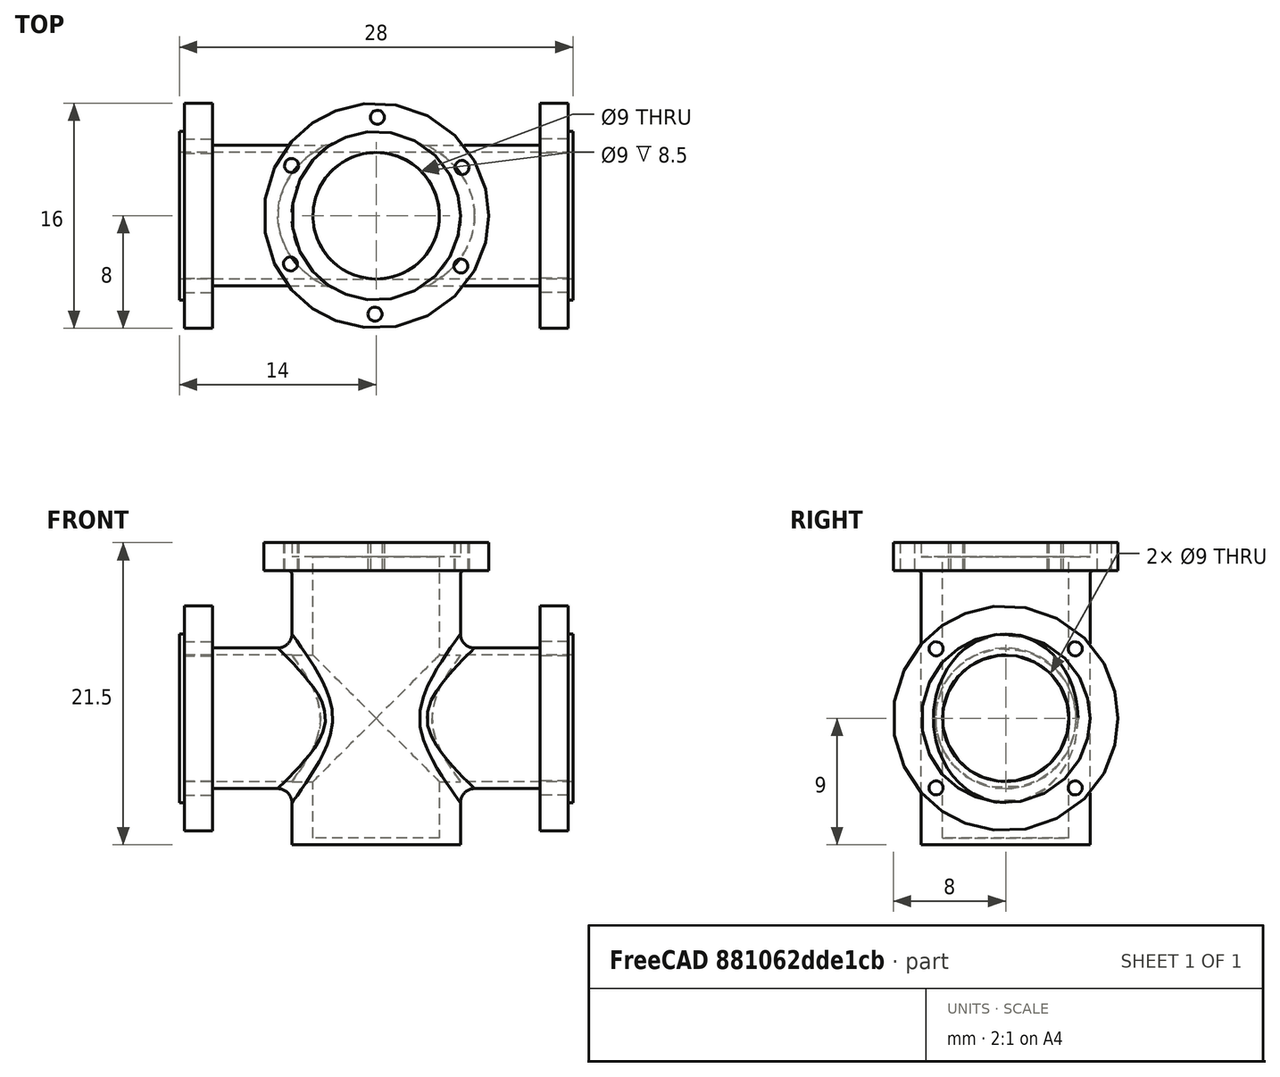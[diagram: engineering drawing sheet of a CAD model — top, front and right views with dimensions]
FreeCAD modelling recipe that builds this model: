
FCSTD DOCUMENT  (FreeCAD 0.17R9652 (Git))
Label: Moderate
License: All rights reserved
LicenseURL: http://en.wikipedia.org/wiki/All_rights_reserved
objects: Sketcher::SketchObject×10, PartDesign::Pad×5, PartDesign::Pocket×5, PartDesign::Mirrored×3, PartDesign::Plane×2, PartDesign::Body×2, PartDesign::Fillet×2, PartDesign::PolarPattern×1, PartDesign::Boolean×1
note: 41 computed .brp shape members not serialized (recipe doc carries the construction recipe); baked Part::Feature solids carry a one-line shape summary decoded from their .brp

FEATURE [Sketcher::SketchObject] Sketch
  MapMode = 5
  Support = -> [XY_Plane]
  sketch-geometry (1):
    g0: Circle CenterX=0 CenterY=0 CenterZ=0 NormalX=0 NormalY=0 NormalZ=1 Radius=6
  constraints (2):
    c: Coincident(g0,g-1)
    c: Radius(g0) = 6
FEATURE [PartDesign::Pad] Pad
  Length = 12
  Length2 = 9
  Midplane = true
  Profile = -> Sketch
  Type = 4
FEATURE [PartDesign::Plane] DatumPlane
  MapMode = 5
  Placement = pos=(0,0,12.5) rot=(0,0,1;0rad)
  Support = -> [XY_Plane]
  superPlacement = pos=(0,0,12.5) rot=(0,0,1;0rad)
FEATURE [Sketcher::SketchObject] Sketch001
  MapMode = 5
  Placement = pos=(0,0,12.5) rot=(0,0,1;0rad)
  Support = -> [DatumPlane]
  sketch-geometry (1):
    g0: Circle CenterX=0 CenterY=0 CenterZ=0 NormalX=0 NormalY=0 NormalZ=1 Radius=8
  constraints (2):
    c: Coincident(g0,g-1)
    c: Radius(g0) = 8
FEATURE [PartDesign::Pad] Pad001
  BaseFeature = -> Pad
  Length = 2
  Length2 = 100
  Profile = -> Sketch001
  Reversed = true
  Type = 0
FEATURE [PartDesign::Body] Body001
  Origin = -> Body001Origin
FEATURE [Sketcher::SketchObject] Sketch005
  MapMode = 5
  Placement = pos=(0,0,0) rot=(0.57735,0.57735,0.57735;2.0944rad)
  Support = -> [YZ_Plane]
  sketch-geometry (1):
    g0: Circle CenterX=0 CenterY=0 CenterZ=0 NormalX=0 NormalY=0 NormalZ=1 Radius=5
  constraints (2):
    c: Coincident(g0,g-1)
    c: Radius(g0) = 5
FEATURE [PartDesign::Pad] Pad002
  Length = 28
  Length2 = 100
  Midplane = true
  Placement = pos=(0,0,0) rot=(0.57735,0.57735,0.57735;2.0944rad)
  Profile = -> Sketch005
  Type = 0
FEATURE [PartDesign::Plane] DatumPlane001
  MapMode = 5
  Placement = pos=(13.65,0,0) rot=(0.57735,0.57735,0.57735;2.0944rad)
  Support = -> [YZ_Plane001]
  superPlacement = pos=(0,0,13.65) rot=(0,0,1;0rad)
FEATURE [Sketcher::SketchObject] Sketch006
  MapMode = 5
  Placement = pos=(13.65,0,0) rot=(0.57735,0.57735,0.57735;2.0944rad)
  Support = -> [DatumPlane001]
  sketch-geometry (1):
    g0: Circle CenterX=0 CenterY=0 CenterZ=0 NormalX=0 NormalY=0 NormalZ=1 Radius=6
  constraints (2):
    c: Coincident(g0,g-1)
    c: Radius(g0) = 6
FEATURE [PartDesign::Pad] Pad003
  BaseFeature = -> Pad002
  Length = 0.35
  Length2 = 100
  Placement = pos=(0,0,0) rot=(0.57735,0.57735,0.57735;2.0944rad)
  Profile = -> Sketch006
  Type = 0
FEATURE [PartDesign::Mirrored] Mirrored
  BaseFeature = -> Pad003
  MirrorPlane = -> YZ_Plane001
  Originals = -> [Pad003]
  Placement = pos=(0,0,0) rot=(0.57735,0.57735,0.57735;2.0944rad)
FEATURE [Sketcher::SketchObject] Sketch007
  MapMode = 5
  Placement = pos=(13.65,0,0) rot=(0.57735,0.57735,0.57735;2.0944rad)
  Support = -> [DatumPlane001]
  sketch-geometry (1):
    g0: Circle CenterX=0 CenterY=0 CenterZ=0 NormalX=0 NormalY=0 NormalZ=1 Radius=8
  constraints (2):
    c: Coincident(g0,g-1)
    c: Radius(g0) = 8
FEATURE [PartDesign::Pad] Pad004
  BaseFeature = -> Mirrored
  Length = 2
  Length2 = 100
  Placement = pos=(0,0,0) rot=(0.57735,0.57735,0.57735;2.0944rad)
  Profile = -> Sketch007
  Reversed = true
  Type = 0
FEATURE [PartDesign::Mirrored] Mirrored001
  BaseFeature = -> Pad004
  MirrorPlane = -> YZ_Plane001
  Originals = -> [Pad004]
  Placement = pos=(0,0,0) rot=(0.57735,0.57735,0.57735;2.0944rad)
FEATURE [Sketcher::SketchObject] Sketch008
  MapMode = 5
  Placement = pos=(13.65,0,0) rot=(0.57735,0.57735,0.57735;2.0944rad)
  Support = -> [DatumPlane001]
  sketch-geometry (9):
    g0: LineSegment [constr] StartX=-4.94975 StartY=4.94975 StartZ=0 EndX=-4.94975 EndY=-4.94975 EndZ=0
    g1: LineSegment [constr] StartX=-4.94975 StartY=-4.94975 StartZ=0 EndX=4.94975 EndY=-4.94975 EndZ=0
    g2: LineSegment [constr] StartX=4.94975 StartY=-4.94975 StartZ=0 EndX=4.94975 EndY=4.94975 EndZ=0
    g3: LineSegment [constr] StartX=4.94975 StartY=4.94975 StartZ=0 EndX=-4.94975 EndY=4.94975 EndZ=0
    g4: Circle [constr] CenterX=0 CenterY=0 CenterZ=0 NormalX=0 NormalY=0 NormalZ=1 Radius=7
    g5: Circle CenterX=-4.94975 CenterY=4.94975 CenterZ=0 NormalX=0 NormalY=0 NormalZ=1 Radius=0.5
    g6: Circle CenterX=4.94975 CenterY=4.94975 CenterZ=0 NormalX=0 NormalY=0 NormalZ=1 Radius=0.5
    g7: Circle CenterX=4.94975 CenterY=-4.94975 CenterZ=0 NormalX=0 NormalY=0 NormalZ=1 Radius=0.5
    g8: Circle CenterX=-4.94975 CenterY=-4.94975 CenterZ=0 NormalX=0 NormalY=0 NormalZ=1 Radius=0.5
  constraints (22):
    c: Coincident(g0,g1)
    c: Coincident(g1,g2)
    c: Coincident(g2,g3)
    c: Coincident(g3,g0)
    c: Equal(g0,g1)
    c: Equal(g0,g2)
    c: Equal(g0,g3)
    c: PointOnObject(g0,g4)
    c: PointOnObject(g1,g4)
    c: PointOnObject(g2,g4)
    c: PointOnObject(g3,g4)
    c: Coincident(g4,g-1)
    c: Horizontal(g3)
    c: Radius(g4) = 7
    c: Coincident(g5,g0)
    c: Coincident(g6,g2)
    c: Coincident(g7,g1)
    c: Coincident(g8,g0)
    c: Equal(g8,g5)
    c: Equal(g5,g6)
    c: Equal(g6,g7)
    c: Radius(g5) = 0.5
FEATURE [PartDesign::Pocket] Pocket003
  BaseFeature = -> Mirrored001
  Length = 2
  Placement = pos=(0,0,0) rot=(0.57735,0.57735,0.57735;2.0944rad)
  Profile = -> Sketch008
  Type = 0
FEATURE [PartDesign::Mirrored] Mirrored002
  BaseFeature = -> Pocket003
  MirrorPlane = -> YZ_Plane001
  Originals = -> [Pocket003]
  Placement = pos=(0,0,0) rot=(0.57735,0.57735,0.57735;2.0944rad)
FEATURE [Sketcher::SketchObject] Sketch010
  MapMode = 5
  Placement = pos=(0,0,12.5) rot=(0,0,1;0rad)
  Support = -> [DatumPlane]
  sketch-geometry (1):
    g0: Circle CenterX=0.081932 CenterY=7 CenterZ=0 NormalX=0 NormalY=0 NormalZ=1 Radius=0.5
  constraints (2):
    c: Radius(g0) = 0.5
    c: DistanceY(g0) = 7
FEATURE [PartDesign::Pocket] Pocket
  BaseFeature = -> Pad001
  Length = 2
  Profile = -> Sketch010
  Type = 0
FEATURE [PartDesign::PolarPattern] PolarPattern
  Angle = 360
  Axis = -> Sketch010 [N_Axis]
  BaseFeature = -> Pocket
  Occurrences = 6
  Originals = -> [Pocket]
FEATURE [Sketcher::SketchObject] Sketch011
  MapMode = 5
  Placement = pos=(0,0,12.5) rot=(0,0,1;0rad)
  Support = -> [DatumPlane]
  sketch-geometry (1):
    g0: Circle CenterX=0 CenterY=0 CenterZ=0 NormalX=0 NormalY=0 NormalZ=1 Radius=6
  constraints (2):
    c: Coincident(g0,g-1)
    c: Radius(g0) = 6
FEATURE [PartDesign::Pocket] Pocket005
  BaseFeature = -> PolarPattern
  Length = 1
  Profile = -> Sketch011
  Type = 0
FEATURE [PartDesign::Fillet] Fillet
  Base = -> Pocket005 [Edge3]
  BaseFeature = -> Pocket005
  Radius = 0.25
FEATURE [PartDesign::Boolean] Boolean
  BaseFeature = -> Fillet
  Bodies = -> [Body001]
  Type = 0
FEATURE [Sketcher::SketchObject] Sketch012
  MapMode = 5
  Placement = pos=(0,0,12.5) rot=(0,0,1;0rad)
  Support = -> [DatumPlane]
  sketch-geometry (1):
    g0: Circle CenterX=0 CenterY=0 CenterZ=0 NormalX=0 NormalY=0 NormalZ=1 Radius=4.5
  constraints (2):
    c: Coincident(g0,g-1)
    c: Radius(g0) = 4.5
FEATURE [PartDesign::Pocket] Pocket006
  BaseFeature = -> Boolean
  Length = 21
  Profile = -> Sketch012
  Type = 0
FEATURE [Sketcher::SketchObject] Sketch013
  MapMode = 5
  Placement = pos=(0,0,0) rot=(0.57735,0.57735,0.57735;2.0944rad)
  Support = -> [YZ_Plane]
  sketch-geometry (1):
    g0: Circle CenterX=0 CenterY=0 CenterZ=0 NormalX=0 NormalY=0 NormalZ=1 Radius=4.5
  constraints (2):
    c: Coincident(g0,g-1)
    c: Radius(g0) = 4.5
FEATURE [PartDesign::Pocket] Pocket007
  BaseFeature = -> Pocket006
  Length = 5
  Midplane = true
  Profile = -> Sketch013
  Type = 1
FEATURE [PartDesign::Fillet] Fillet001
  Base = -> Pocket007 [Edge3,Edge6,Edge7,Edge8]
  BaseFeature = -> Pocket007
  Radius = 1
FEATURE [PartDesign::Body] Body
  Origin = -> BodyOrigin
  Tip = -> Fillet001
